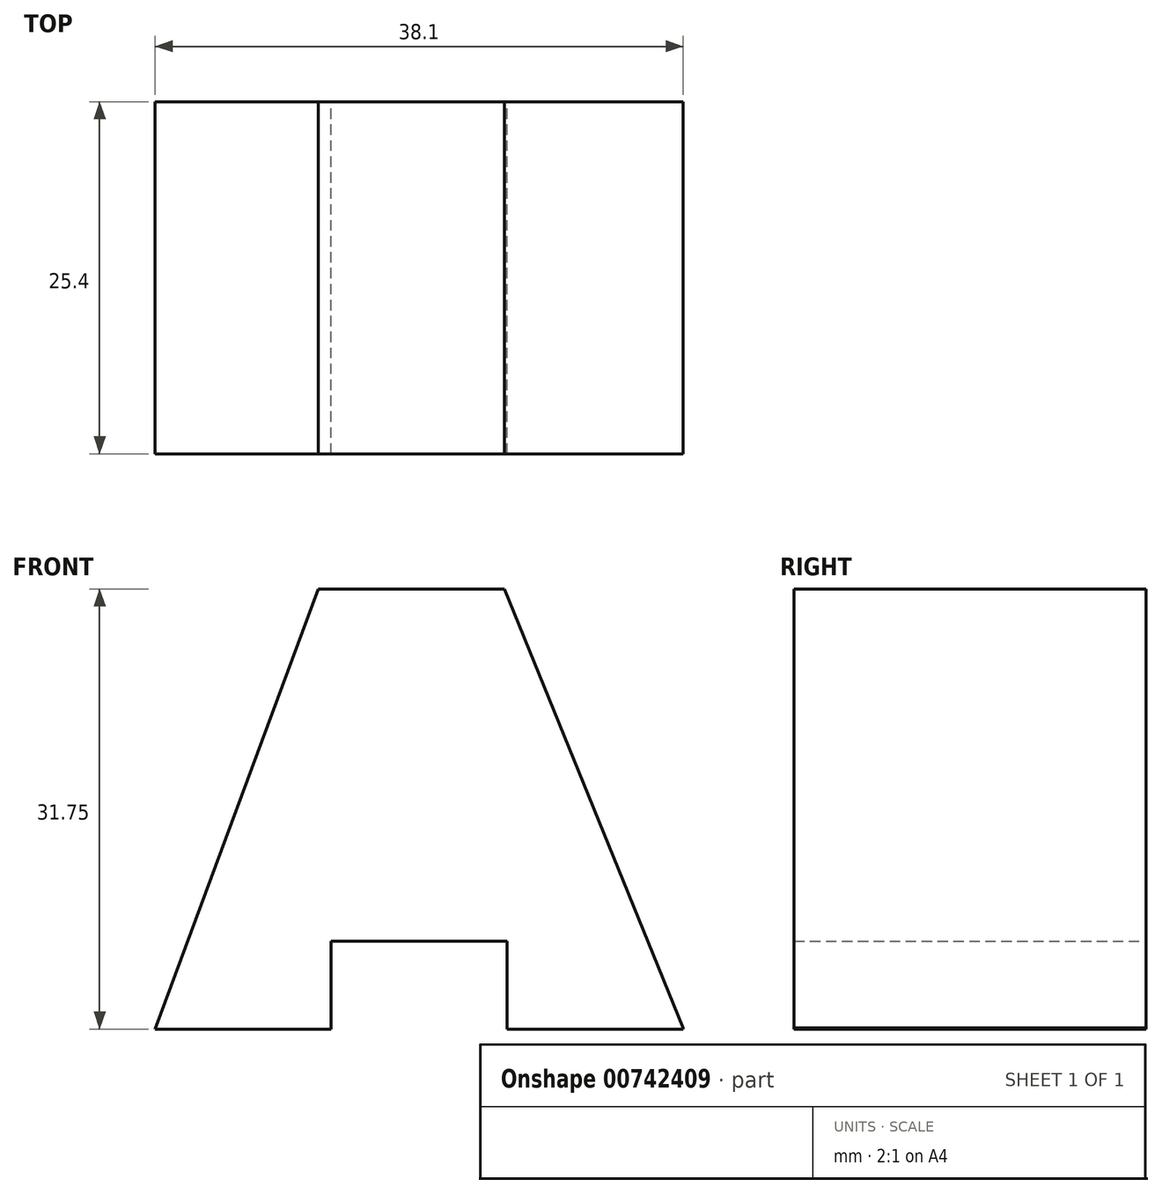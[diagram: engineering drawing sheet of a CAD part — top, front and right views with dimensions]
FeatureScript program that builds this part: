
annotation { "Feature Type Name" : "Feature", "Feature Type Description" : "" }
export const myFeature = defineFeature(function(context is Context, id is Id, definition is map)
    precondition{}
    {
        {
            var Q0;
            Q0=qCreatedBy(makeId("Front.planeOp"),FACE);
            var sketch = newSketch(context, id + "F0", { "sketchPlane" : qUnion([Q0])});
            skLineSegment(sketch, "E0", {"start": v(0, 31.75) * mm, "end": v(0, 0) * mm});
            skLineSegment(sketch, "E1", {"start": v(0, 0) * mm, "end": v(38.1, 0) * mm});
            skLineSegment(sketch, "E2", {"start": v(38.1, 0) * mm, "end": v(38.1, 31.75) * mm});
            skLineSegment(sketch, "E3", {"start": v(38.1, 31.75) * mm, "end": v(0, 31.75) * mm});
            skSolve(sketch);
        }
        {
            var Q0;
            Q0 = qSketchRegion(id + "F0", true);
            extrude(context, id + "F1", {"entities" : qUnion([Q0]), "depth" : 25.4 * mm, "offsetDistance" : 25.4 * mm});
        }
        {
            var Q0;
            Q0=qCreatedBy(makeId("Front.planeOp"),FACE);
            var sketch = newSketch(context, id + "F2", { "sketchPlane" : qUnion([Q0])});
            skLineSegment(sketch, "E4", {"start": v(12.7, 0) * mm, "end": v(12.7, 6.35) * mm});
            skLineSegment(sketch, "E5", {"start": v(12.7, 6.35) * mm, "end": v(25.4, 6.35) * mm});
            skLineSegment(sketch, "E6", {"start": v(25.4, 6.35) * mm, "end": v(25.4, 0) * mm});
            skLineSegment(sketch, "E7", {"start": v(12.7, 0) * mm, "end": v(25.4, 0) * mm});
            skSolve(sketch);
        }
        {
            var Q0;
            Q0 = qSketchRegion(id + "F2", true);
            extrude(context, id + "F3", {"entities" : qUnion([Q0]), "operationType" : NewBodyOperationType.REMOVE, "endBound" : BoundingType.THROUGH_ALL, "depth" : 25.4 * mm, "offsetDistance" : 25.4 * mm});
        }
        {
            var Q0;
            Q0=qCreatedBy(makeId("Front.planeOp"),FACE);
            var sketch = newSketch(context, id + "F4", { "sketchPlane" : qUnion([Q0])});
            skLineSegment(sketch, "E8", {"start": v(11.81, 31.89) * mm, "end": v(0, 0) * mm});
            skLineSegment(sketch, "E9", {"start": v(25.07, 32.08) * mm, "end": v(38.13, 0) * mm});
            skLineSegment(sketch, "E10", {"start": v(11.81, 31.89) * mm, "end": v(0, 31.89) * mm});
            skLineSegment(sketch, "E11", {"start": v(0, 31.89) * mm, "end": v(0, 0) * mm});
            skLineSegment(sketch, "E12", {"start": v(25.07, 32.08) * mm, "end": v(38.13, 32.08) * mm});
            skLineSegment(sketch, "E13", {"start": v(38.13, 32.08) * mm, "end": v(38.13, 0) * mm});
            skSolve(sketch);
        }
        {
            var Q0;
            Q0 = qSketchRegion(id + "F4", true);
            extrude(context, id + "F5", {"entities" : qUnion([Q0]), "operationType" : NewBodyOperationType.REMOVE, "endBound" : BoundingType.THROUGH_ALL, "depth" : 25.4 * mm, "offsetDistance" : 25.4 * mm});
        }
    });
